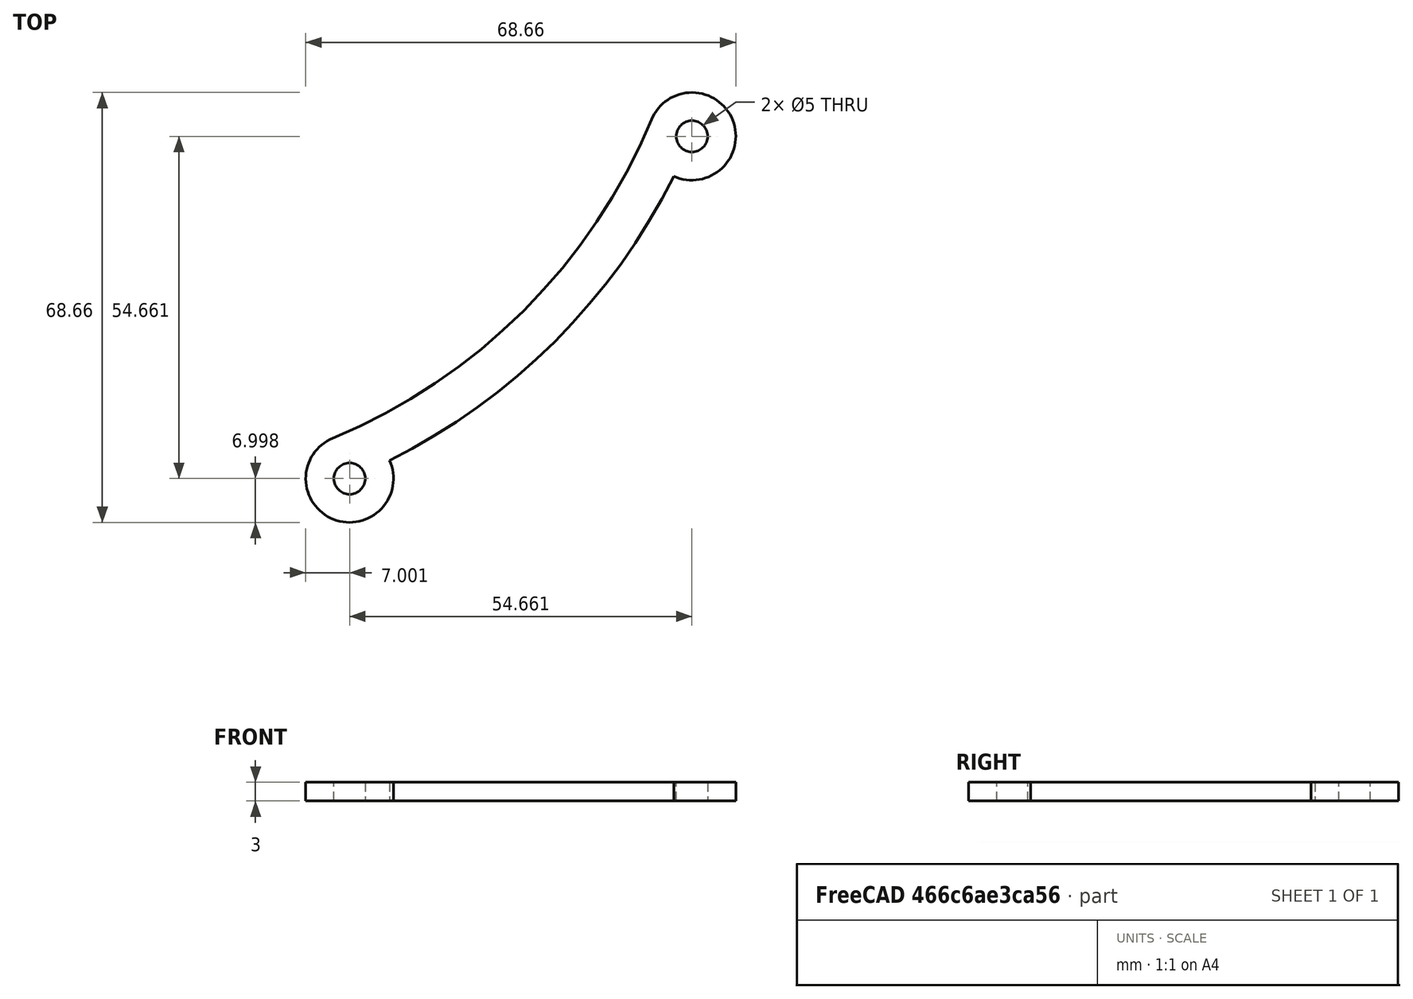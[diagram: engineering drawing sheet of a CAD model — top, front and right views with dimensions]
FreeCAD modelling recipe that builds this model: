
FCSTD DOCUMENT  (FreeCAD 0.19R24276 (Git))
Label: Out_gear_support
License: All rights reserved
LicenseURL: http://en.wikipedia.org/wiki/All_rights_reserved
objects: Sketcher::SketchObject×1, PartDesign::Pad×1, PartDesign::Body×1
note: 4 computed .brp shape members not serialized (recipe doc carries the construction recipe); baked Part::Feature solids carry a one-line shape summary decoded from their .brp

FEATURE [Sketcher::SketchObject] Sketch001
  FullyConstrained = true
  MapMode = 5
  Placement = pos=(0,0,0) rot=(1,0,0;3.14159rad)
  sketch-geometry (10):
    g0: LineSegment StartX=0 StartY=0 StartZ=0 EndX=93.3118 EndY=38.651 EndZ=0
    g1: LineSegment StartX=0 StartY=0 StartZ=0 EndX=38.651 EndY=93.3118 EndZ=0
    g2: Circle CenterX=38.651 CenterY=93.3118 CenterZ=0 NormalX=0 NormalY=0 NormalZ=1 AngleXU=0 Radius=2.5
    g3: Circle CenterX=93.3118 CenterY=38.651 CenterZ=0 NormalX=0 NormalY=0 NormalZ=1 AngleXU=0 Radius=2.5
    g4: ArcOfCircle CenterX=38.651 CenterY=93.3118 CenterZ=0 NormalX=0 NormalY=0 NormalZ=1 AngleXU=0 Radius=7 StartAngle=5.85583 EndAngle=10.6029
    g5: LineSegment StartX=38.651 StartY=93.3118 StartZ=0 EndX=35.9722 EndY=86.8447 EndZ=0
    g6: ArcOfCircle CenterX=0 CenterY=0 CenterZ=0 NormalX=0 NormalY=0 NormalZ=1 AngleXU=0 Radius=94 StartAngle=0.392699 EndAngle=1.1781
    g7: ArcOfCircle CenterX=0 CenterY=0 CenterZ=0 NormalX=0 NormalY=0 NormalZ=1 AngleXU=0 Radius=101 StartAngle=1.24742 EndAngle=6.60656
    g8: ArcOfCircle CenterX=93.3118 CenterY=38.651 CenterZ=0 NormalX=0 NormalY=0 NormalZ=1 AngleXU=0 Radius=7 StartAngle=3.53429 EndAngle=8.28134
    g9: ArcOfCircle CenterX=0 CenterY=0 CenterZ=0 NormalX=0 NormalY=0 NormalZ=1 AngleXU=0 Radius=101 StartAngle=0.46202 EndAngle=1.10878
  constraints (29):
    c: Angle(g-1,g0) = 0.392699
    c: Angle(g0,g1) = 0.785398
    c: Coincident(g2,g1)
    c: Coincident(g3,g0)
    c: Coincident(g4,g2)
    c: Coincident(g5,g2)
    c: Parallel(g5,g1)
    c: Diameter(g4) = 14
    c: PointOnObject(g6,g4)
    c: PointOnObject(g6,g0)
    c: PointOnObject(g4,g6)
    c: Diameter(g2) = 5
    c: Equal(g2,g3)
    c: Diameter(g6) = 188
    c: Coincident(g7,g6)
    c: PointOnObject(g3,g7)
    c: Diameter(g7) = 202
    c: Coincident(g8,g3)
    c: Coincident(g0,g-1)
    c: Coincident(g0,g1)
    c: Coincident(g6,g-1)
    c: Coincident(g4,g5)
    c: Coincident(g9,g4)
    c: Coincident(g8,g6)
    c: Equal(g7,g9)
    c: Coincident(g9,g8)
    c: Coincident(g7,g9)
    c: PointOnObject(g7,g8)
    c: PointOnObject(g7,g4)
FEATURE [PartDesign::Pad] Pad
  Direction = (1,1,1)
  Length = 3
  Length2 = 100
  Placement = pos=(0,0,0) rot=(1,0,0;3.14159rad)
  Profile = -> Sketch001
  Type = 0
FEATURE [PartDesign::Body] Body
  Group = -> [Sketch001,Pad]
  Origin = -> Origin
  Tip = -> Pad
